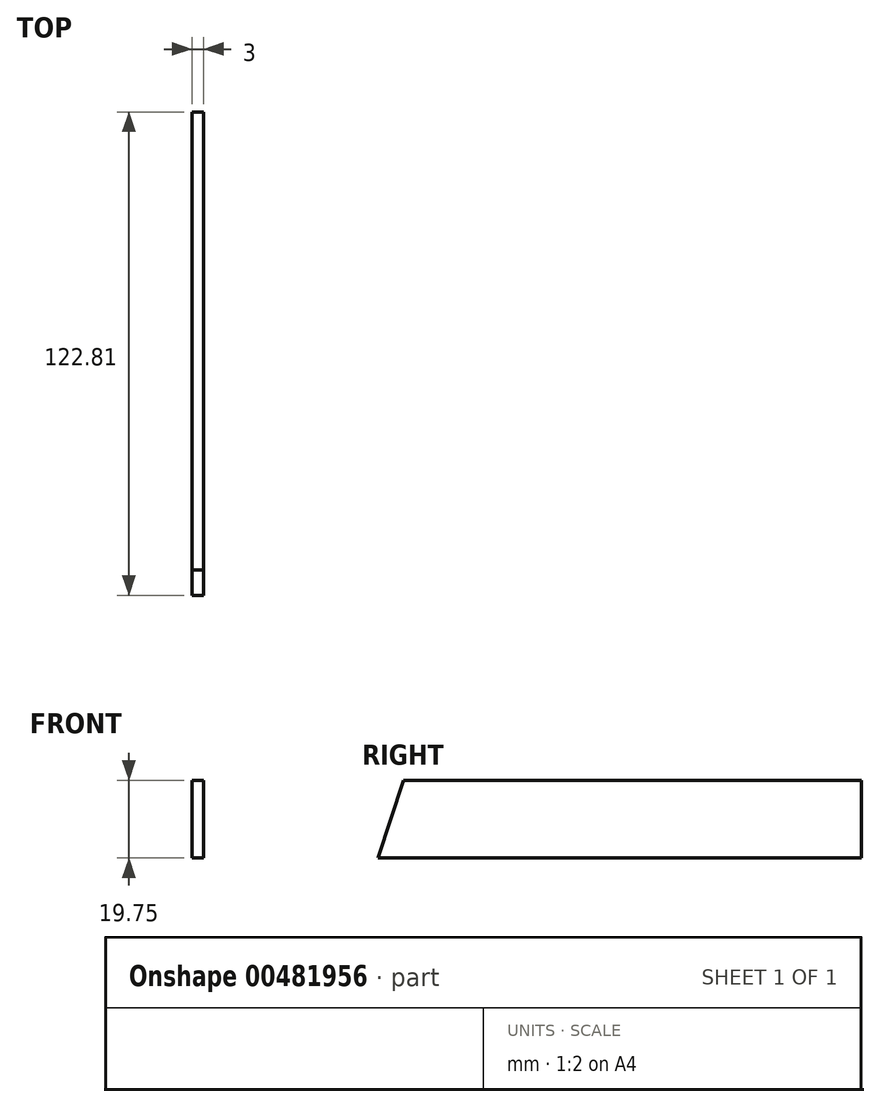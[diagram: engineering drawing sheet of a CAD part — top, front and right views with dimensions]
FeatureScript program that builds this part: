
annotation { "Feature Type Name" : "Feature", "Feature Type Description" : "" }
export const myFeature = defineFeature(function(context is Context, id is Id, definition is map)
    precondition{}
    {
        {
            var Q0;
            Q0=qCreatedBy(makeId("Right.planeOp"),FACE);
            var sketch = newSketch(context, id + "F0", { "sketchPlane" : qUnion([Q0])});
            skLineSegment(sketch, "E0", {"start": v(0, 0) * mm, "end": v(-122.81, 0) * mm});
            skLineSegment(sketch, "E1", {"start": v(-122.81, 0) * mm, "end": v(-116.39, 19.75) * mm});
            skLineSegment(sketch, "E2", {"start": v(-116.39, 19.75) * mm, "end": v(0, 19.75) * mm});
            skPoint(sketch, "E3.orphan", {"position": v(0, 50.7) * mm});
            skPoint(sketch, "E4.end.orphan", {"position": v(-0.6, 0) * mm});
            skPoint(sketch, "E4.start.orphan", {"position": v(-4.27, 19.75) * mm});
            skLineSegment(sketch, "E5", {"start": v(0, 0) * mm, "end": v(0, 19.75) * mm});
            skPoint(sketch, "E6.start.orphan", {"position": v(107.85, 19.75) * mm});
            skPoint(sketch, "E7.orphan", {"position": v(121.6, 0) * mm});
            skSolve(sketch);
        }
        {
            var Q0;
            Q0 = qSketchRegion(id + "F0", true);
            extrude(context, id + "F1", {"entities" : qUnion([Q0]), "depth" : 3 * mm, "offsetDistance" : 25 * mm});
        }
    });
